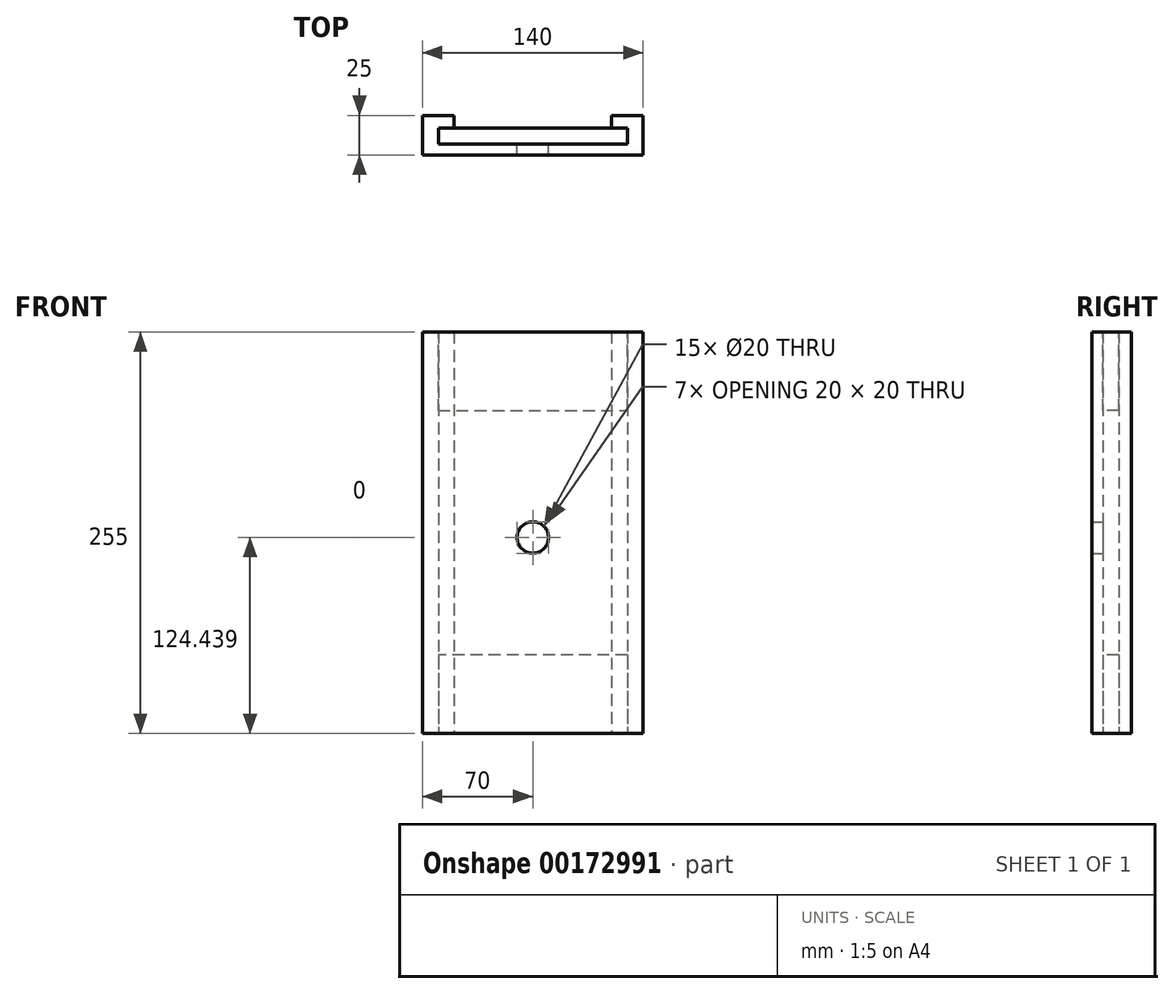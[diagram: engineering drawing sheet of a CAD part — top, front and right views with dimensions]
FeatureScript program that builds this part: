
annotation { "Feature Type Name" : "Feature", "Feature Type Description" : "" }
export const myFeature = defineFeature(function(context is Context, id is Id, definition is map)
    precondition{}
    {
        {
            var Q0;
            Q0=qCreatedBy(makeId("Top.planeOp"),FACE);
            var sketch = newSketch(context, id + "F0", { "sketchPlane" : qUnion([Q0])});
            skLineSegment(sketch, "E0", {"start": v(0, 0) * mm, "end": v(70, 0) * mm});
            skLineSegment(sketch, "E1", {"start": v(70, 0) * mm, "end": v(70, 25) * mm});
            skLineSegment(sketch, "E2", {"start": v(70, 25) * mm, "end": v(50, 25) * mm});
            skLineSegment(sketch, "E3", {"start": v(50, 25) * mm, "end": v(50, 17) * mm});
            skLineSegment(sketch, "E4", {"start": v(50, 17) * mm, "end": v(60, 17) * mm});
            skLineSegment(sketch, "E5", {"start": v(60, 17) * mm, "end": v(60, 7) * mm});
            skLineSegment(sketch, "E6", {"start": v(60, 7) * mm, "end": v(0, 7) * mm});
            skLineSegment(sketch, "E7", {"start": v(0, 7) * mm, "end": v(0, 0) * mm, "construction": true});
            skLineSegment(sketch, "E8.MirrorCS", {"start": v(-60, 7) * mm, "end": v(0, 7) * mm});
            skLineSegment(sketch, "E9.MirrorCS", {"start": v(0, 0) * mm, "end": v(-70, 0) * mm});
            skLineSegment(sketch, "E10.MirrorCS", {"start": v(-60, 17) * mm, "end": v(-60, 7) * mm});
            skLineSegment(sketch, "E11.MirrorCS", {"start": v(-70, 0) * mm, "end": v(-70, 25) * mm});
            skLineSegment(sketch, "E12.MirrorCS", {"start": v(-50, 25) * mm, "end": v(-50, 17) * mm});
            skLineSegment(sketch, "E13.MirrorCS", {"start": v(-70, 25) * mm, "end": v(-50, 25) * mm});
            skLineSegment(sketch, "E14.MirrorCS", {"start": v(-50, 17) * mm, "end": v(-60, 17) * mm});
            skSolve(sketch);
        }
        {
            var Q0;
            {var subQ1=sQuery(id+"F0.wireOp",EDGE,"E8.MirrorCS");Q0=makeQuery(id+"F0.imprint","IMPRINT",FACE,{"disambiguationData":[TD([[makeQuery(id+"F0.imprint","IMPRINT",EDGE,{"derivedFrom":subQ1}),-1.0]])]});}
            var Q1;
            {var subQ0=sQuery(id+"F0.wireOp",EDGE,"E0");Q1=makeQuery(id+"F0.imprint","IMPRINT",FACE,{"disambiguationData":[TD([[makeQuery(id+"F0.imprint","IMPRINT",EDGE,{"derivedFrom":subQ0}),1.0]])]});}
            extrude(context, id + "F1", {"entities" : qUnion([Q0, Q1]), "depth" : 255 * mm});
        }
        {
            var Q0;
            Q0=makeQuery(id+"F1.opExtrude","SWEPT_FACE",FACE,{"disambiguationData":[OSD([sQuery(id+"F0.wireOp",EDGE,"E6"),sQuery(id+"F0.wireOp",EDGE,"E8.MirrorCS")])]});
            var sketch = newSketch(context, id + "F2", { "sketchPlane" : qUnion([Q0])});
            skCircle(sketch, "E15", {"center": v(0, 124.44) * mm, "radius": 10 * mm});
            skSolve(sketch);
        }
        {
            var Q0;
            Q0=makeQuery(id+"F2.imprint","IMPRINT",FACE,{"disambiguationData":[TD([[makeQuery(id+"F2.imprint","IMPRINT",EDGE,{"derivedFrom":sQuery(id+"F2.wireOp",EDGE,"E15")}),1.0]])]});
            extrude(context, id + "F3", {"entities" : qUnion([Q0]), "operationType" : NewBodyOperationType.REMOVE, "oppositeDirection" : true, "depth" : 12 * mm});
        }
        {
            var Q0;
            Q0=makeQuery(id+"F1.opExtrude","CAP_FACE",FACE,{"disambiguationData":[OSD([sQuery(id+"F0.wireOp",EDGE,"E0"),sQuery(id+"F0.wireOp",EDGE,"E1"),sQuery(id+"F0.wireOp",EDGE,"E2"),sQuery(id+"F0.wireOp",EDGE,"E3"),sQuery(id+"F0.wireOp",EDGE,"E4"),sQuery(id+"F0.wireOp",EDGE,"E5"),sQuery(id+"F0.wireOp",EDGE,"E6"),sQuery(id+"F0.wireOp",EDGE,"E8.MirrorCS"),sQuery(id+"F0.wireOp",EDGE,"E9.MirrorCS"),sQuery(id+"F0.wireOp",EDGE,"E10.MirrorCS"),sQuery(id+"F0.wireOp",EDGE,"E11.MirrorCS"),sQuery(id+"F0.wireOp",EDGE,"E12.MirrorCS"),sQuery(id+"F0.wireOp",EDGE,"E13.MirrorCS"),sQuery(id+"F0.wireOp",EDGE,"E14.MirrorCS")])],"isStart":false});
            var sketch = newSketch(context, id + "F4", { "sketchPlane" : qUnion([Q0])});
            skLineSegment(sketch, "E16", {"start": v(-50, 17) * mm, "end": v(-60, 17) * mm});
            skLineSegment(sketch, "E17", {"start": v(-60, 17) * mm, "end": v(-60, 7) * mm});
            skLineSegment(sketch, "E18", {"start": v(-60, 7) * mm, "end": v(60, 7) * mm});
            skLineSegment(sketch, "E19", {"start": v(60, 7) * mm, "end": v(60, 17) * mm});
            skLineSegment(sketch, "E20", {"start": v(60, 17) * mm, "end": v(50, 17) * mm});
            skLineSegment(sketch, "E21", {"start": v(50, 17) * mm, "end": v(-50, 17) * mm});
            skSolve(sketch);
        }
        {
            var Q0;
            Q0=makeQuery(id+"F4.imprint","IMPRINT",FACE,{"disambiguationData":[TD([[makeQuery(id+"F4.imprint","IMPRINT",EDGE,{"derivedFrom":sQuery(id+"F4.wireOp",EDGE,"E16")}),1.0]])]});
            extrude(context, id + "F5", {"entities" : qUnion([Q0]), "oppositeDirection" : true, "depth" : 50 * mm});
        }
        {
            var Q0;
            Q0=makeQuery(id+"F1.opExtrude","CAP_FACE",FACE,{"disambiguationData":[OSD([sQuery(id+"F0.wireOp",EDGE,"E0"),sQuery(id+"F0.wireOp",EDGE,"E1"),sQuery(id+"F0.wireOp",EDGE,"E2"),sQuery(id+"F0.wireOp",EDGE,"E3"),sQuery(id+"F0.wireOp",EDGE,"E4"),sQuery(id+"F0.wireOp",EDGE,"E5"),sQuery(id+"F0.wireOp",EDGE,"E6"),sQuery(id+"F0.wireOp",EDGE,"E8.MirrorCS"),sQuery(id+"F0.wireOp",EDGE,"E9.MirrorCS"),sQuery(id+"F0.wireOp",EDGE,"E10.MirrorCS"),sQuery(id+"F0.wireOp",EDGE,"E11.MirrorCS"),sQuery(id+"F0.wireOp",EDGE,"E12.MirrorCS"),sQuery(id+"F0.wireOp",EDGE,"E13.MirrorCS"),sQuery(id+"F0.wireOp",EDGE,"E14.MirrorCS")])],"isStart":true});
            var sketch = newSketch(context, id + "F6", { "sketchPlane" : qUnion([Q0])});
            skLineSegment(sketch, "E22", {"start": v(-60, -7) * mm, "end": v(-60, -17) * mm});
            skLineSegment(sketch, "E23", {"start": v(-60, -17) * mm, "end": v(-50, -17) * mm});
            skLineSegment(sketch, "E24", {"start": v(-50, -17) * mm, "end": v(50, -17) * mm});
            skLineSegment(sketch, "E25", {"start": v(50, -17) * mm, "end": v(60, -17) * mm});
            skLineSegment(sketch, "E26", {"start": v(60, -17) * mm, "end": v(60, -7) * mm});
            skLineSegment(sketch, "E27", {"start": v(60, -7) * mm, "end": v(-60, -7) * mm});
            skSolve(sketch);
        }
        {
            var Q0;
            Q0=makeQuery(id+"F6.imprint","IMPRINT",FACE,{"disambiguationData":[TD([[makeQuery(id+"F6.imprint","IMPRINT",EDGE,{"derivedFrom":sQuery(id+"F6.wireOp",EDGE,"E22")}),-1.0]])]});
            extrude(context, id + "F7", {"entities" : qUnion([Q0]), "oppositeDirection" : true, "depth" : 50 * mm});
        }
    });
